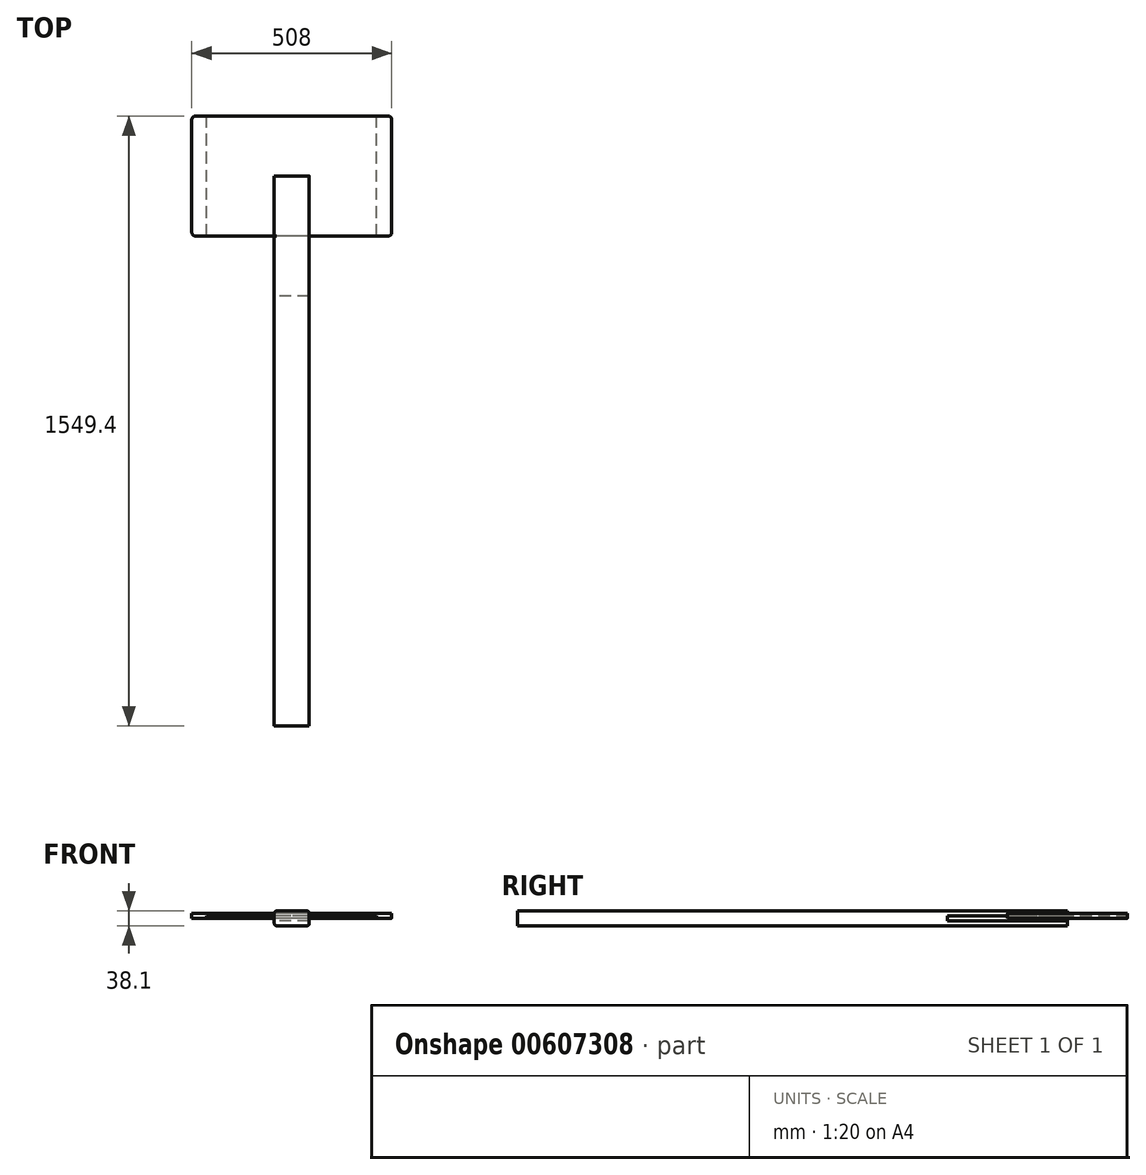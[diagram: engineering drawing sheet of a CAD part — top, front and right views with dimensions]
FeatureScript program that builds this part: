
annotation { "Feature Type Name" : "Feature", "Feature Type Description" : "" }
export const myFeature = defineFeature(function(context is Context, id is Id, definition is map)
    precondition{}
    {
        {
            var Q0;
            Q0=qCreatedBy(makeId("Front.planeOp"),FACE);
            var sketch = newSketch(context, id + "F0", { "sketchPlane" : qUnion([Q0])});
            skLineSegment(sketch, "E0.bottom", {"start": v(44.45, -6.35) * mm, "end": v(-44.45, -6.35) * mm});
            skLineSegment(sketch, "E0.top", {"start": v(44.45, 6.35) * mm, "end": v(-44.45, 6.35) * mm});
            skLineSegment(sketch, "E0.left", {"start": v(44.45, -6.35) * mm, "end": v(44.45, 6.35) * mm});
            skLineSegment(sketch, "E0.right", {"start": v(-44.45, -6.35) * mm, "end": v(-44.45, 6.35) * mm});
            skPoint(sketch, "E0.middle", {"position": v(0, 0) * mm});
            skSolve(sketch);
        }
        {
            var Q0;
            Q0=qCreatedBy(makeId("Front.planeOp"),FACE);
            var sketch = newSketch(context, id + "F1", { "sketchPlane" : qUnion([Q0])});
            skLineSegment(sketch, "E1.bottom", {"start": v(38.1, -19.05) * mm, "end": v(-38.1, -19.05) * mm});
            skLineSegment(sketch, "E1.top", {"start": v(38.1, 19.05) * mm, "end": v(-38.1, 19.05) * mm});
            skLineSegment(sketch, "E1.left", {"start": v(44.45, -12.7) * mm, "end": v(44.45, 12.7) * mm});
            skLineSegment(sketch, "E1.right", {"start": v(-44.45, -12.7) * mm, "end": v(-44.45, 12.7) * mm});
            skPoint(sketch, "E1.middle", {"position": v(0, 0) * mm});
            skPoint(sketch, "E2.visualSharp", {"position": v(-44.45, 19.05) * mm});
            skArc(sketch, "E2.filletArc", {"start": v(-38.1, 19.05) * mm, "mid": v(-42.6, 17.2) * mm, "end": v(-44.45, 12.7) * mm});
            skPoint(sketch, "E3.visualSharp", {"position": v(-44.45, -19.05) * mm});
            skArc(sketch, "E3.filletArc", {"start": v(-44.45, -12.7) * mm, "mid": v(-42.6, -17.2) * mm, "end": v(-38.1, -19.05) * mm});
            skPoint(sketch, "E4.visualSharp", {"position": v(44.45, -19.05) * mm});
            skArc(sketch, "E4.filletArc", {"start": v(38.1, -19.05) * mm, "mid": v(42.6, -17.2) * mm, "end": v(44.45, -12.7) * mm});
            skPoint(sketch, "E5.visualSharp", {"position": v(44.45, 19.05) * mm});
            skArc(sketch, "E5.filletArc", {"start": v(44.45, 12.7) * mm, "mid": v(42.6, 17.2) * mm, "end": v(38.1, 19.05) * mm});
            skSolve(sketch);
        }
        {
            var Q0;
            Q0=makeQuery(id+"F1.imprint","IMPRINT",FACE,{"disambiguationData":[TD([[makeQuery(id+"F1.imprint","IMPRINT",EDGE,{"derivedFrom":sQuery(id+"F1.wireOp",EDGE,"E1.bottom")}),-1.0]])]});
            extrude(context, id + "F2", {"entities" : qUnion([Q0]), "depth" : 1397 * mm, "offsetDistance" : 25.4 * mm});
        }
        {
            var Q0;
            Q0=makeQuery(id+"F0.imprint","IMPRINT",FACE,{"disambiguationData":[TD([[makeQuery(id+"F0.imprint","IMPRINT",EDGE,{"derivedFrom":sQuery(id+"F0.wireOp",EDGE,"E0.bottom")}),-1.0]])]});
            extrude(context, id + "F3", {"entities" : qUnion([Q0]), "depth" : 304.8 * mm, "offsetDistance" : 25.4 * mm});
        }
        {
            var Q0;
            Q0=qCreatedBy(makeId("Top.planeOp"),FACE);
            var sketch = newSketch(context, id + "F4", { "sketchPlane" : qUnion([Q0])});
            skLineSegment(sketch, "E6.bottom", {"start": v(254, -152.4) * mm, "end": v(-254, -152.4) * mm});
            skLineSegment(sketch, "E6.top", {"start": v(254, 152.4) * mm, "end": v(-254, 152.4) * mm});
            skLineSegment(sketch, "E6.left", {"start": v(254, -152.4) * mm, "end": v(254, 152.4) * mm});
            skLineSegment(sketch, "E6.right", {"start": v(-254, -152.4) * mm, "end": v(-254, 152.4) * mm});
            skPoint(sketch, "E6.middle", {"position": v(0, 0) * mm});
            skSolve(sketch);
        }
        {
            var Q0;
            Q0=makeQuery(id+"F4.imprint","IMPRINT",FACE,{"disambiguationData":[TD([[makeQuery(id+"F4.imprint","IMPRINT",EDGE,{"derivedFrom":sQuery(id+"F4.wireOp",EDGE,"E6.bottom")}),-1.0]])]});
            extrude(context, id + "F5", {"entities" : qUnion([Q0]), "depth" : 12.7 * mm, "offsetDistance" : 25.4 * mm});
        }
        {
            var Q0;
            Q0=qCreatedBy(makeId("Top.planeOp"),FACE);
            var sketch = newSketch(context, id + "F6", { "sketchPlane" : qUnion([Q0])});
            skLineSegment(sketch, "E7.bottom", {"start": v(215.9, -152.4) * mm, "end": v(-215.9, -152.4) * mm});
            skLineSegment(sketch, "E7.top", {"start": v(215.9, 152.4) * mm, "end": v(-215.9, 152.4) * mm});
            skLineSegment(sketch, "E7.left", {"start": v(215.9, -152.4) * mm, "end": v(215.9, 152.4) * mm});
            skLineSegment(sketch, "E7.right", {"start": v(-215.9, -152.4) * mm, "end": v(-215.9, 152.4) * mm});
            skPoint(sketch, "E7.middle", {"position": v(0, 0) * mm});
            skSolve(sketch);
        }
        {
            var Q0;
            Q0=makeQuery(id+"F6.imprint","IMPRINT",FACE,{"disambiguationData":[TD([[makeQuery(id+"F6.imprint","IMPRINT",EDGE,{"derivedFrom":sQuery(id+"F6.wireOp",EDGE,"E7.bottom")}),-1.0]])]});
            extrude(context, id + "F7", {"entities" : qUnion([Q0]), "depth" : 6.35 * mm, "offsetDistance" : 25.4 * mm});
        }
        {
            var Q0;
            Q0=makeQuery(id+"F5.opExtrude","SWEPT_EDGE",EDGE,{"disambiguationData":[OSD([sQuery(id+"F4.wireOp",EDGE,"E6.bottom"),sQuery(id+"F4.wireOp",EDGE,"E6.left")])]});
            var Q1;
            Q1=makeQuery(id+"F5.opExtrude","SWEPT_EDGE",EDGE,{"disambiguationData":[OSD([sQuery(id+"F4.wireOp",EDGE,"E6.top"),sQuery(id+"F4.wireOp",EDGE,"E6.left")])]});
            var Q2;
            Q2=makeQuery(id+"F5.opExtrude","SWEPT_EDGE",EDGE,{"disambiguationData":[OSD([sQuery(id+"F4.wireOp",EDGE,"E6.bottom"),sQuery(id+"F4.wireOp",EDGE,"E6.right")])]});
            var Q3;
            Q3=makeQuery(id+"F5.opExtrude","SWEPT_EDGE",EDGE,{"disambiguationData":[OSD([sQuery(id+"F4.wireOp",EDGE,"E6.top"),sQuery(id+"F4.wireOp",EDGE,"E6.right")])]});
            fillet(context, id + "F8", {"entities" : qUnion([Q0, Q1, Q2, Q3]), "radius" : 9.2 * mm, "tangentPropagation" : true, "allowEdgeOverflow" : false});
        }
    });
